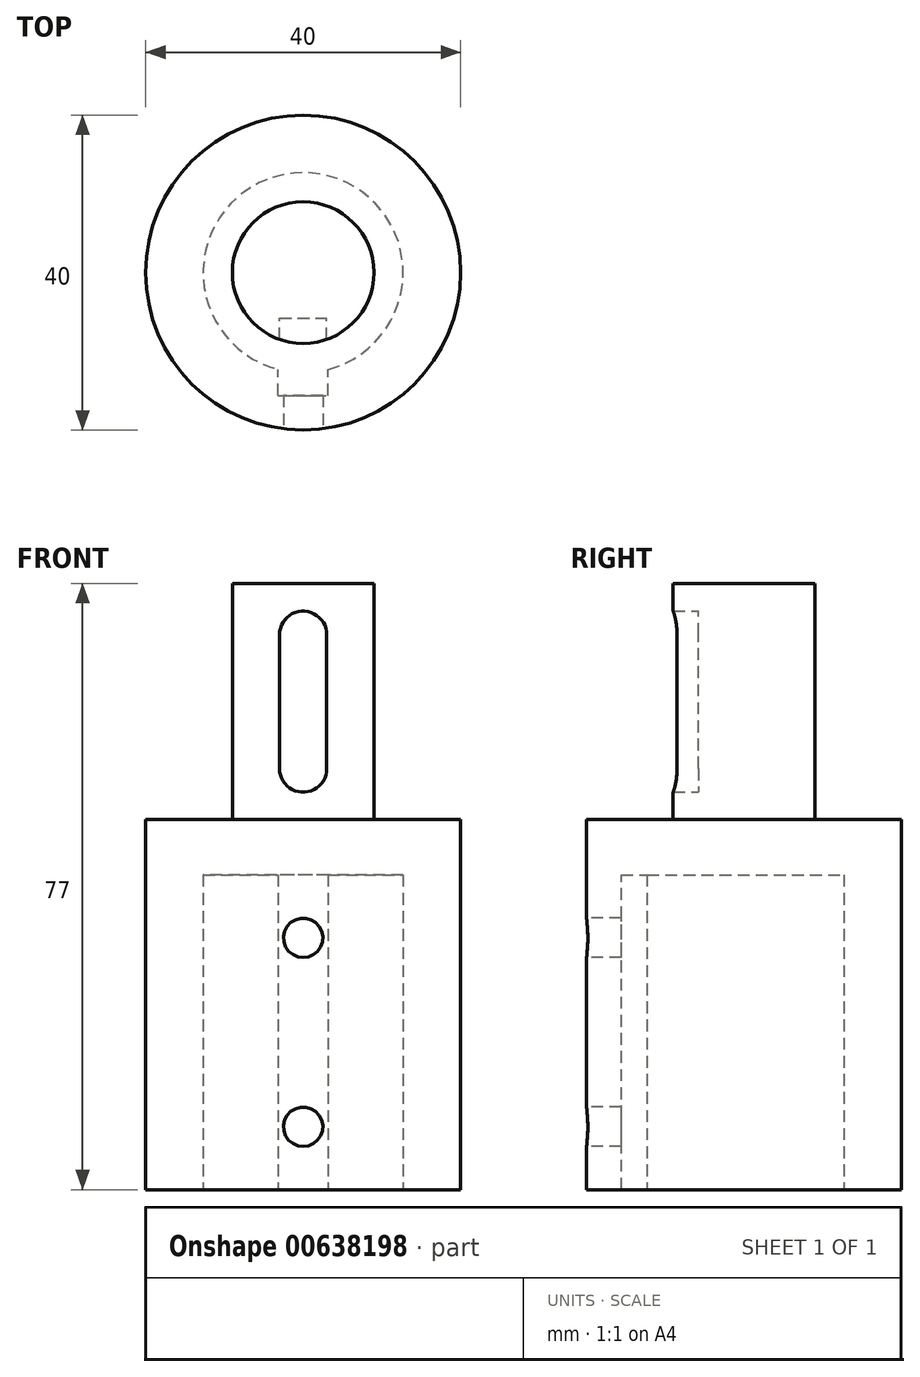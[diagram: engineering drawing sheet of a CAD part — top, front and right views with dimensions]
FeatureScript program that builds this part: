
annotation { "Feature Type Name" : "Feature", "Feature Type Description" : "" }
export const myFeature = defineFeature(function(context is Context, id is Id, definition is map)
    precondition{}
    {
        {
            var Q0;
            Q0=qCreatedBy(makeId("Top.planeOp"),FACE);
            var sketch = newSketch(context, id + "F0", { "sketchPlane" : qUnion([Q0])});
            skCircle(sketch, "E0", {"center": v(0, 0) * mm, "radius": 20 * mm});
            skCircle(sketch, "E1", {"center": v(0, 0) * mm, "radius": 9 * mm});
            skCircle(sketch, "E2", {"center": v(0, 0) * mm, "radius": 12.7 * mm});
            skSolve(sketch);
        }
        {
            var Q0;
            Q0=makeQuery(id+"F0.imprint","IMPRINT",FACE,{"disambiguationData":[TD([[makeQuery(id+"F0.imprint","IMPRINT",EDGE,{"derivedFrom":sQuery(id+"F0.wireOp",EDGE,"E0")}),1.0]])]});
            var Q1;
            Q1=makeQuery(id+"F0.imprint","IMPRINT",FACE,{"disambiguationData":[TD([[makeQuery(id+"F0.imprint","IMPRINT",EDGE,{"derivedFrom":sQuery(id+"F0.wireOp",EDGE,"E1")}),-1.0]])]});
            extrude(context, id + "F1", {"entities" : qUnion([Q0, Q1]), "depth" : 47 * mm, "offsetDistance" : 25 * mm});
        }
        {
            var Q0;
            Q0=makeQuery(id+"F0.imprint","IMPRINT",FACE,{"disambiguationData":[TD([[makeQuery(id+"F0.imprint","IMPRINT",EDGE,{"derivedFrom":sQuery(id+"F0.wireOp",EDGE,"E1")}),1.0]])]});
            extrude(context, id + "F2", {"entities" : qUnion([Q0]), "operationType" : NewBodyOperationType.ADD, "depth" : 77 * mm, "offsetDistance" : 25 * mm});
        }
        {
            var Q0;
            Q0=makeQuery(id+"F0.imprint","IMPRINT",FACE,{"disambiguationData":[TD([[makeQuery(id+"F0.imprint","IMPRINT",EDGE,{"derivedFrom":sQuery(id+"F0.wireOp",EDGE,"E1")}),1.0]])]});
            var Q1;
            Q1=makeQuery(id+"F0.imprint","IMPRINT",FACE,{"disambiguationData":[TD([[makeQuery(id+"F0.imprint","IMPRINT",EDGE,{"derivedFrom":sQuery(id+"F0.wireOp",EDGE,"E1")}),-1.0]])]});
            extrude(context, id + "F3", {"entities" : qUnion([Q0, Q1]), "operationType" : NewBodyOperationType.REMOVE, "depth" : 40 * mm, "offsetDistance" : 25.4 * mm});
        }
        {
            var Q0;
            Q0=qCreatedBy(makeId("Front.planeOp"),FACE);
            var sketch = newSketch(context, id + "F4", { "sketchPlane" : qUnion([Q0])});
            skLineSegment(sketch, "E3", {"start": v(0, 0) * mm, "end": v(3.17, 0) * mm});
            skLineSegment(sketch, "E4", {"start": v(3.17, 0) * mm, "end": v(3.17, 40) * mm});
            skLineSegment(sketch, "E5", {"start": v(3.17, 40) * mm, "end": v(-3.18, 40) * mm});
            skLineSegment(sketch, "E6", {"start": v(-3.18, 40) * mm, "end": v(-3.17, 0) * mm});
            skLineSegment(sketch, "E7", {"start": v(-3.18, 0) * mm, "end": v(0, 0) * mm});
            skSolve(sketch);
        }
        {
            var Q0;
            Q0=makeQuery(id+"F4.imprint","IMPRINT",FACE,{"disambiguationData":[TD([[makeQuery(id+"F4.imprint","IMPRINT",EDGE,{"derivedFrom":sQuery(id+"F4.wireOp",EDGE,"E3")}),1.0]])]});
            extrude(context, id + "F5", {"entities" : qUnion([Q0]), "operationType" : NewBodyOperationType.REMOVE, "depth" : 15.6 * mm, "offsetDistance" : 25.4 * mm});
        }
        {
            var Q0;
            Q0=qCreatedBy(makeId("Front.planeOp"),FACE);
            var sketch = newSketch(context, id + "F6", { "sketchPlane" : qUnion([Q0])});
            skLineSegment(sketch, "E8", {"start": v(0, 73.5) * mm, "end": v(3, 73.5) * mm});
            skLineSegment(sketch, "E9", {"start": v(3, 73.5) * mm, "end": v(3, 50.5) * mm});
            skLineSegment(sketch, "E10", {"start": v(3, 50.5) * mm, "end": v(0, 50.5) * mm});
            skLineSegment(sketch, "E11", {"start": v(0, 50.5) * mm, "end": v(-3, 50.5) * mm});
            skLineSegment(sketch, "E12", {"start": v(-3, 50.5) * mm, "end": v(-3, 73.5) * mm});
            skLineSegment(sketch, "E13", {"start": v(-3, 73.5) * mm, "end": v(0, 73.5) * mm});
            skCircle(sketch, "E14", {"center": v(0, 70.5) * mm, "radius": 3 * mm});
            skPoint(sketch, "E14.second.point", {"position": v(0, 64) * mm});
            skPoint(sketch, "E14.third.point", {"position": v(3, 67) * mm});
            skCircle(sketch, "E15", {"center": v(0, 53.5) * mm, "radius": 3 * mm});
            skPoint(sketch, "E15.second.point", {"position": v(0, 53) * mm});
            skPoint(sketch, "E15.third.point", {"position": v(3, 50) * mm});
            skSolve(sketch);
        }
        {
            var Q0;
            {var subQ0=sQuery(id+"F6.wireOp",EDGE,"E14");var subQ1=sQuery(id+"F6.wireOp",EDGE,"E9");var subQ2=makeQuery(id+"F6.imprint","INTERSECT",VERTEX,{"derivedFrom":[subQ1,subQ0]});Q0=makeQuery(id+"F6.imprint","IMPRINT",FACE,{"disambiguationData":[TD([[makeQuery(id+"F6.imprint","IMPRINT",EDGE,{"disambiguationData":[TD([[subQ2,-1.0]])],"derivedFrom":subQ1}),-1.0]])]});}
            var Q1;
            {var subQ0=sQuery(id+"F6.wireOp",EDGE,"E15");var subQ1=makeQuery(id+"F6.imprint","INTERSECT",VERTEX,{"derivedFrom":[sQuery(id+"F6.wireOp",EDGE,"E9"),subQ0]});Q1=makeQuery(id+"F6.imprint","IMPRINT",FACE,{"disambiguationData":[TD([[makeQuery(id+"F6.imprint","IMPRINT",EDGE,{"disambiguationData":[TD([[subQ1,-1.0]])],"derivedFrom":subQ0}),1.0]])]});}
            var Q2;
            {var subQ0=sQuery(id+"F6.wireOp",EDGE,"E14");var subQ2=makeQuery(id+"F6.imprint","INTERSECT",VERTEX,{"derivedFrom":[sQuery(id+"F6.wireOp",EDGE,"E9"),subQ0]});Q2=makeQuery(id+"F6.imprint","IMPRINT",FACE,{"disambiguationData":[TD([[makeQuery(id+"F6.imprint","IMPRINT",EDGE,{"disambiguationData":[TD([[subQ2,1.0]])],"derivedFrom":subQ0}),1.0]])]});}
            var Q3;
            Q3=sQuery(id+"F6.wireOp",EDGE,"E15");
            var Q4;
            Q4=sQuery(id+"F6.wireOp",EDGE,"E12");
            var Q5;
            Q5=sQuery(id+"F6.wireOp",EDGE,"E9");
            var Q6;
            Q6=sQuery(id+"F6.wireOp",EDGE,"E14");
            extrude(context, id + "F7", {"entities" : qUnion([Q0, Q1, Q2]), "operationType" : NewBodyOperationType.REMOVE, "surfaceEntities" : qUnion([Q3, Q4, Q5, Q6]), "depth" : 9 * mm, "offsetDistance" : 25 * mm, "hasSecondDirection" : true, "secondDirectionOppositeDirection" : true, "secondDirectionDepth" : -5.8 * mm});
        }
        {
            var Q0;
            Q0=qCreatedBy(makeId("Front.planeOp"),FACE);
            var sketch = newSketch(context, id + "F8", { "sketchPlane" : qUnion([Q0])});
            skCircle(sketch, "E16", {"center": v(0, 8) * mm, "radius": 2.5 * mm});
            skCircle(sketch, "E17", {"center": v(0, 32) * mm, "radius": 2.5 * mm});
            skLineSegment(sketch, "E18", {"start": v(0, 8) * mm, "end": v(0, 0) * mm});
            skLineSegment(sketch, "E19", {"start": v(0, 32) * mm, "end": v(0, 0) * mm});
            skSolve(sketch);
        }
        {
            var Q0;
            Q0 = qSketchRegion(id + "F8", true);
            extrude(context, id + "F9", {"entities" : qUnion([Q0]), "operationType" : NewBodyOperationType.REMOVE, "oppositeDirection" : true, "depth" : 0.8 * mm, "offsetDistance" : 25 * mm, "hasSecondDirection" : true, "secondDirectionOppositeDirection" : false, "secondDirectionDepth" : 25 * mm});
        }
    });
